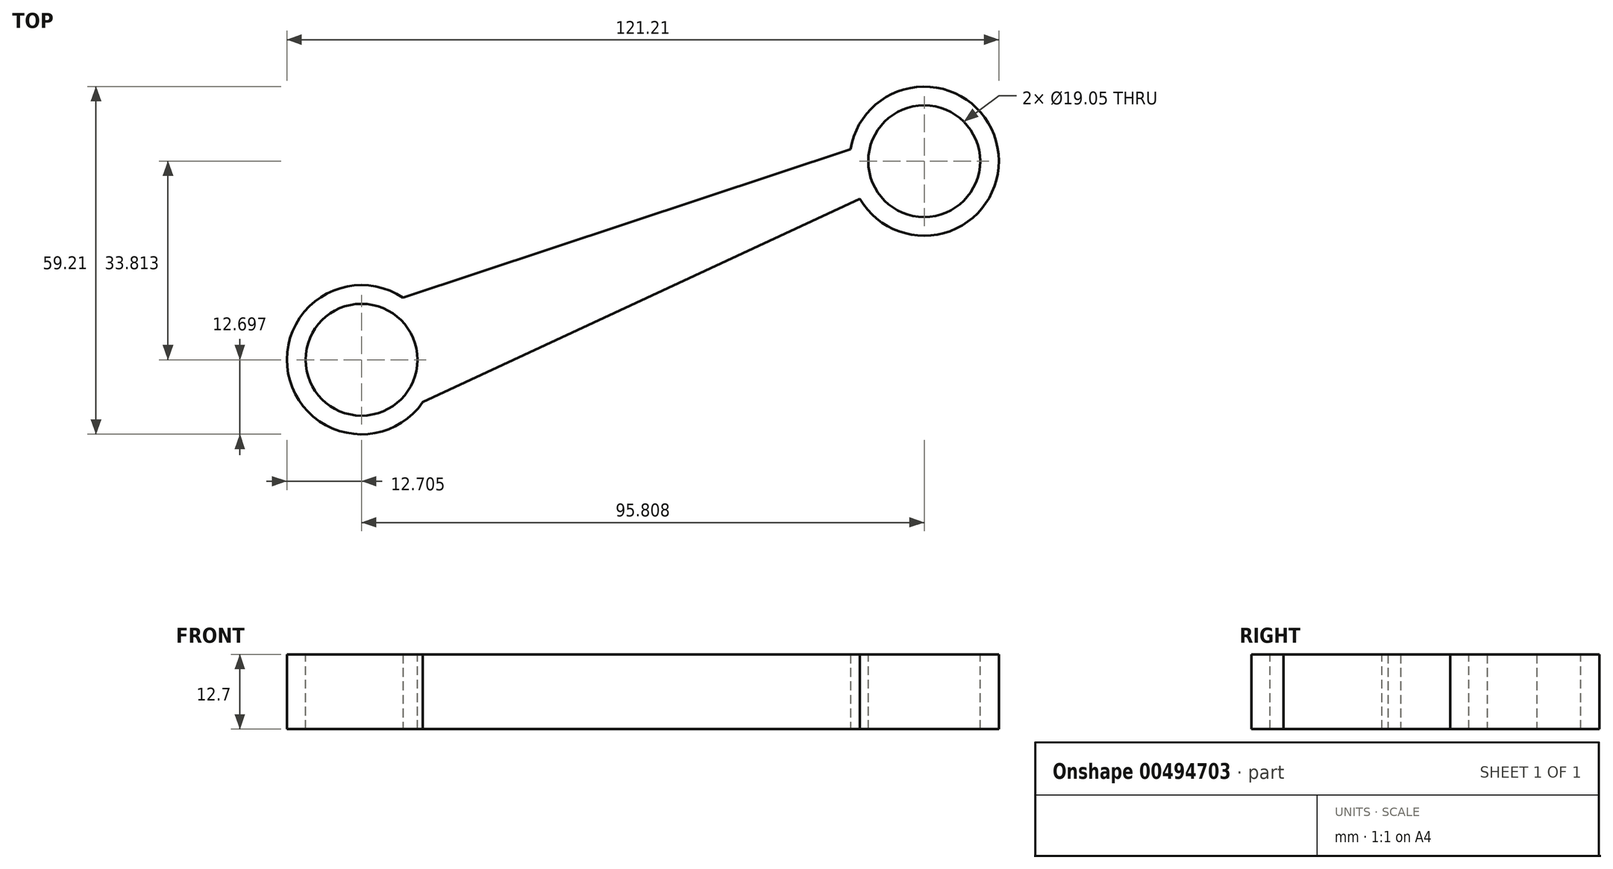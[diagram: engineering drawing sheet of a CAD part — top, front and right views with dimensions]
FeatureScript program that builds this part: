
annotation { "Feature Type Name" : "Feature", "Feature Type Description" : "" }
export const myFeature = defineFeature(function(context is Context, id is Id, definition is map)
    precondition{}
    {
        {
            var Q0;
            Q0=qCreatedBy(makeId("Top.planeOp"),FACE);
            var sketch = newSketch(context, id + "F0", { "sketchPlane" : qUnion([Q0])});
            skCircle(sketch, "E0", {"center": v(-51.67, 20.32) * mm, "radius": 12.7 * mm});
            skCircle(sketch, "E1", {"center": v(44.14, 54.13) * mm, "radius": 12.7 * mm});
            skLineSegment(sketch, "E2", {"start": v(31.6, 56.16) * mm, "end": v(-44.6, 30.87) * mm});
            skLineSegment(sketch, "E3", {"start": v(33.17, 47.74) * mm, "end": v(-41.22, 13.09) * mm});
            skSolve(sketch);
        }
        {
            var Q0;
            {var subQ0=sQuery(id+"F0.wireOp",EDGE,"E0");var subQ1=makeQuery(id+"F0.imprint","INTERSECT",VERTEX,{"derivedFrom":[subQ0,sQuery(id+"F0.wireOp",EDGE,"E2")]});Q0=makeQuery(id+"F0.imprint","IMPRINT",FACE,{"disambiguationData":[TD([[makeQuery(id+"F0.imprint","IMPRINT",EDGE,{"disambiguationData":[TD([[subQ1,-1.0]])],"derivedFrom":subQ0}),1.0]])]});}
            var Q1;
            {var subQ0=sQuery(id+"F0.wireOp",EDGE,"E2");Q1=makeQuery(id+"F0.imprint","IMPRINT",FACE,{"disambiguationData":[TD([[makeQuery(id+"F0.imprint","IMPRINT",EDGE,{"derivedFrom":subQ0}),1.0]])]});}
            var Q2;
            {var subQ0=sQuery(id+"F0.wireOp",EDGE,"E1");var subQ1=makeQuery(id+"F0.imprint","INTERSECT",VERTEX,{"derivedFrom":[subQ0,sQuery(id+"F0.wireOp",EDGE,"E2")]});Q2=makeQuery(id+"F0.imprint","IMPRINT",FACE,{"disambiguationData":[TD([[makeQuery(id+"F0.imprint","IMPRINT",EDGE,{"disambiguationData":[TD([[subQ1,-1.0]])],"derivedFrom":subQ0}),1.0]])]});}
            extrude(context, id + "F1", {"entities" : qUnion([Q0, Q1, Q2]), "depth" : 12.7 * mm});
        }
        {
            var Q0;
            Q0=makeQuery(id+"F1.opExtrude","CAP_FACE",FACE,{"disambiguationData":[OSD([sQuery(id+"F0.wireOp",EDGE,"E0"),sQuery(id+"F0.wireOp",EDGE,"E1"),sQuery(id+"F0.wireOp",EDGE,"E2"),sQuery(id+"F0.wireOp",EDGE,"E3")])],"isStart":false});
            var sketch = newSketch(context, id + "F2", { "sketchPlane" : qUnion([Q0])});
            skCircle(sketch, "E4", {"center": v(-51.67, 20.32) * mm, "radius": 9.53 * mm});
            skCircle(sketch, "E5", {"center": v(44.14, 54.13) * mm, "radius": 9.53 * mm});
            skSolve(sketch);
        }
        {
            var Q0;
            Q0=sQuery(id+"F2.wireOp",VERTEX,"E4.center");
            var Q1;
            Q1=sQuery(id+"F2.wireOp",VERTEX,"E5.center");
            var Q2;
            Q2=makeQuery(id+"F1.opExtrude","SWEPT_BODY",BODY,{"disambiguationData":[OSD([sQuery(id+"F0.wireOp",EDGE,"E0"),sQuery(id+"F0.wireOp",EDGE,"E1"),sQuery(id+"F0.wireOp",EDGE,"E2"),sQuery(id+"F0.wireOp",EDGE,"E3")])]});
            hole(context, id + "F3", {"style" : HoleStyle.SIMPLE, "endStyle" : HoleEndStyle.THROUGH, "holeDiameter" : 19.05 * mm, "isTappedThrough" : true, "tappedDepth" : 12.7 * mm, "tapClearance" : 3, "locations" : qUnion([Q0, Q1]), "scope" : qUnion([Q2])});
        }
    });
